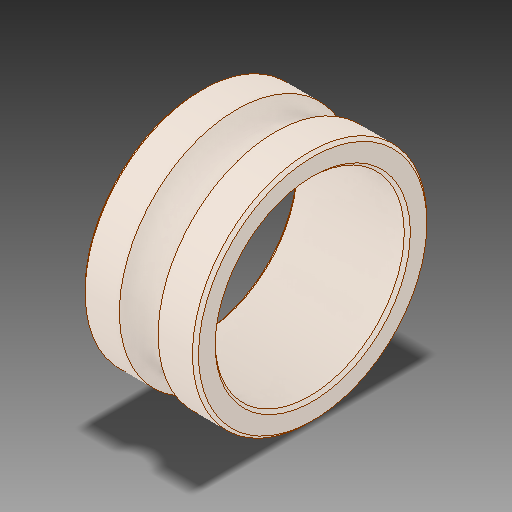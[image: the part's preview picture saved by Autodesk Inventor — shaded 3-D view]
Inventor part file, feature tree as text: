
AUTODESK INVENTOR PART (.ipt)
format: ipt  version: 2017.3 (Build 213256000, 256)  size: 164,352 bytes
history: mixed  units: mm
features: chamfer x1, imported_body x1
ambient origin geometry x8: Origin, YZ Plane, XZ Plane, XY Plane, X Axis, Y Axis, Z Axis, Center Point
bodies: Solid1 (imported_parasolid)
feature tree (2):
  chamfer  "Chamfer2"  [1 undecoded]
  imported_body  NMx_Import_Brep_tag  [imported B-rep: ~10 faces, bbox_mm=[3.0, 6.2, 0.0]]
note: 1 required parameter value undecoded (feature->parameter linkage not recoverable at this tier; creation-order binding heuristic only, values carry confidence <= 0.55)
